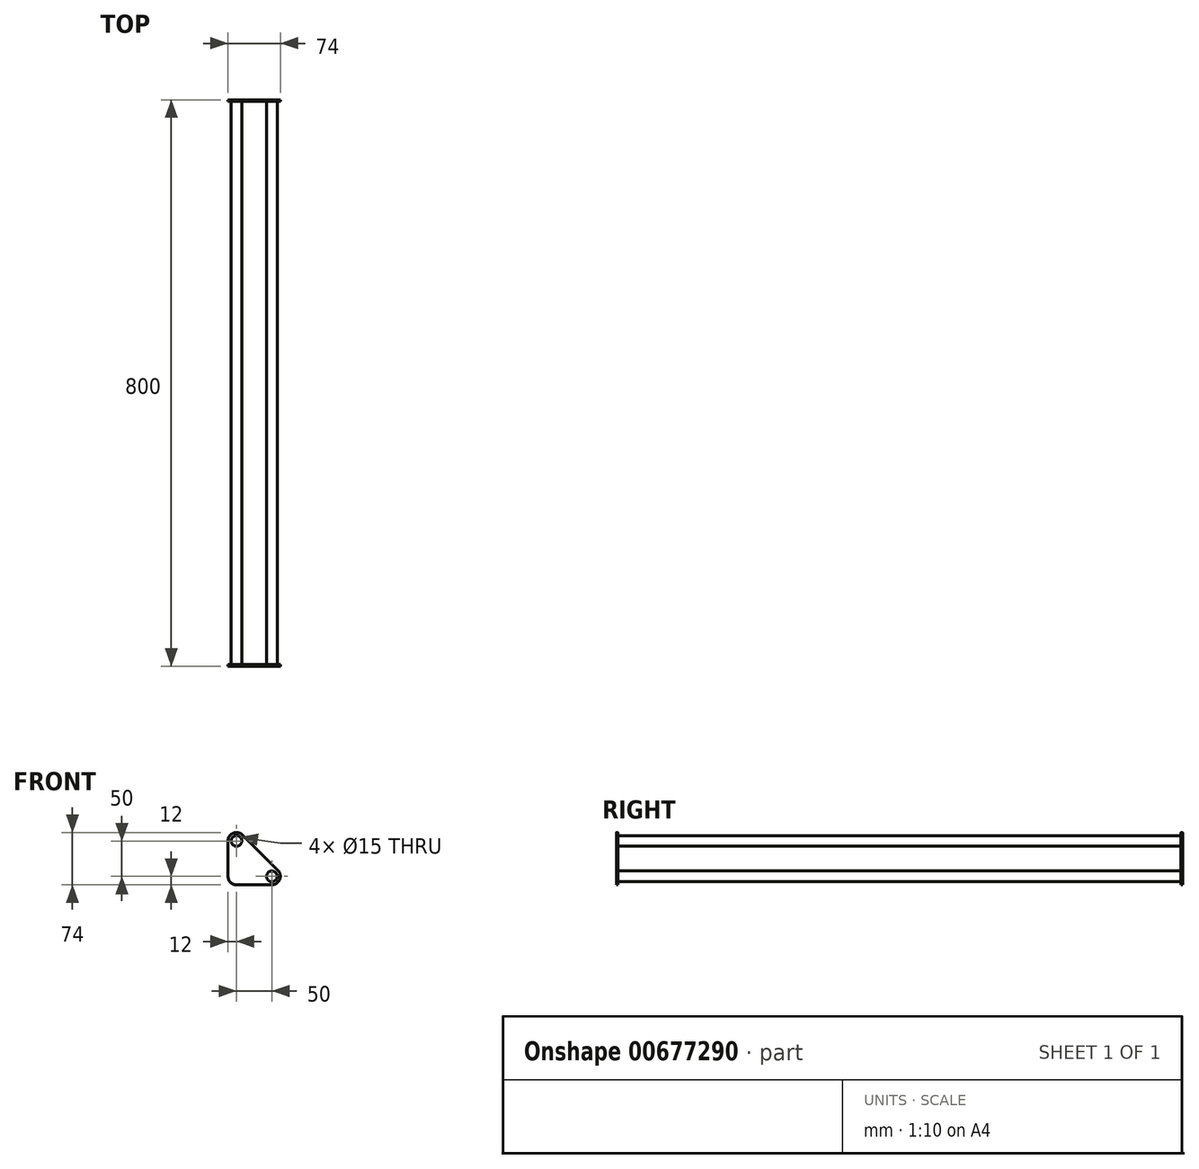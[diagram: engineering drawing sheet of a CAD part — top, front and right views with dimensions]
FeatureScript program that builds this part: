
annotation { "Feature Type Name" : "Feature", "Feature Type Description" : "" }
export const myFeature = defineFeature(function(context is Context, id is Id, definition is map)
    precondition{}
    {
        {
            var Q0;
            Q0=qCreatedBy(makeId("Front.planeOp"),FACE);
            var sketch = newSketch(context, id + "F0", { "sketchPlane" : qUnion([Q0])});
            skCircle(sketch, "E0", {"center": v(0, 0) * mm, "radius": 7.5 * mm});
            skCircle(sketch, "E1", {"center": v(-50, 50) * mm, "radius": 7.5 * mm});
            skSolve(sketch);
        }
        {
            var Q0;
            Q0 = qSketchRegion(id + "F0", true);
            extrude(context, id + "F1", {"entities" : qUnion([Q0]), "depth" : 400 * mm, "offsetDistance" : 25 * mm, "hasSecondDirection" : true, "secondDirectionOppositeDirection" : true, "secondDirectionDepth" : 400 * mm});
        }
        {
            var Q0;
            Q0=makeQuery(id+"F1.opExtrude","CAP_FACE",FACE,{"disambiguationData":[OSD([sQuery(id+"F0.wireOp",EDGE,"E1")])],"isStart":true});
            var sketch = newSketch(context, id + "F2", { "sketchPlane" : qUnion([Q0])});
            skLineSegment(sketch, "E2", {"start": v(-8.49, 8.49) * mm, "end": v(41.51, 58.49) * mm});
            skLineSegment(sketch, "E3", {"start": v(62, 50) * mm, "end": v(62, 0) * mm});
            skLineSegment(sketch, "E4", {"start": v(0, -12) * mm, "end": v(50, -12) * mm});
            skPoint(sketch, "E5.visualSharp", {"position": v(62, 78.97) * mm});
            skArc(sketch, "E5.filletArc", {"start": v(62, 50) * mm, "mid": v(54.6, 61.09) * mm, "end": v(41.51, 58.49) * mm});
            skPoint(sketch, "E6.visualSharp", {"position": v(-28.97, -12) * mm});
            skPoint(sketch, "E7.visualSharp", {"position": v(62, -12) * mm});
            skArc(sketch, "E7.filletArc", {"start": v(50, -12) * mm, "mid": v(58.49, -8.49) * mm, "end": v(62, 0) * mm});
            skCircle(sketch, "E8", {"center": v(0, 0) * mm, "radius": 7.5 * mm});
            skArc(sketch, "E9.filletArc", {"start": v(-8.49, 8.49) * mm, "mid": v(-11.09, -4.6) * mm, "end": v(0, -12) * mm});
            skCircle(sketch, "E10.0", {"center": v(50, 50) * mm, "radius": 7.5 * mm});
            skSolve(sketch);
        }
        {
            var Q0;
            Q0 = qSketchRegion(id + "F2", true);
            extrude(context, id + "F3", {"entities" : qUnion([Q0]), "oppositeDirection" : true, "depth" : 2 * mm, "offsetDistance" : 25 * mm});
        }
        {
            var Q0;
            Q0=makeQuery(id+"F3.opExtrude","SWEPT_BODY",BODY,{"disambiguationData":[OSD([sQuery(id+"F2.wireOp",EDGE,"E2"),sQuery(id+"F2.wireOp",EDGE,"E3"),sQuery(id+"F2.wireOp",EDGE,"E4"),sQuery(id+"F2.wireOp",EDGE,"E5.filletArc"),sQuery(id+"F2.wireOp",EDGE,"E7.filletArc"),sQuery(id+"F2.wireOp",EDGE,"E8"),sQuery(id+"F2.wireOp",EDGE,"E9.filletArc"),sQuery(id+"F2.wireOp",EDGE,"E10.0")])]});
            var Q1;
            Q1=qCreatedBy(makeId("Front.planeOp"),FACE);
            mirror(context, id + "F4", {"entities" : qUnion([Q0]), "mirrorPlane" : qUnion([Q1])});
        }
    });
